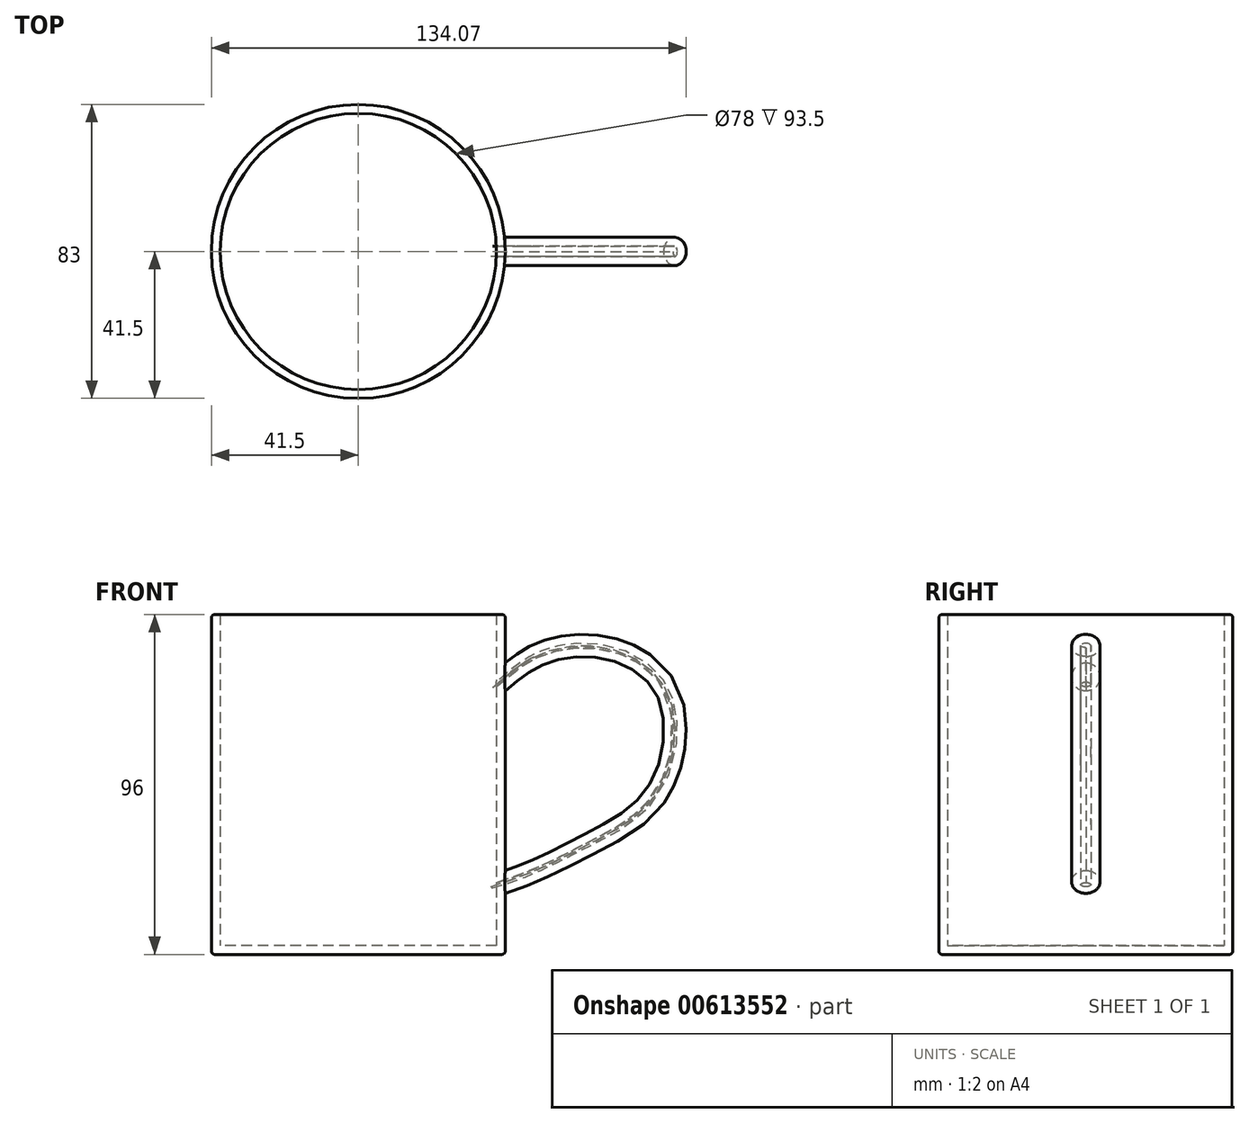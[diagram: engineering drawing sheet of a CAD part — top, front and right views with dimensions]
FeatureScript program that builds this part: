
annotation { "Feature Type Name" : "Feature", "Feature Type Description" : "" }
export const myFeature = defineFeature(function(context is Context, id is Id, definition is map)
    precondition{}
    {
        {
            var Q0;
            Q0=qCreatedBy(makeId("Top.planeOp"),FACE);
            var sketch = newSketch(context, id + "F0", { "sketchPlane" : qUnion([Q0])});
            skCircle(sketch, "E0", {"center": v(0, 0) * mm, "radius": 41.5 * mm});
            skSolve(sketch);
        }
        {
            var Q0;
            Q0 = qSketchRegion(id + "F0", true);
            extrude(context, id + "F1", {"entities" : qUnion([Q0]), "depth" : 96 * mm, "offsetDistance" : 25 * mm});
        }
        {
            var Q0;
            Q0=qCreatedBy(makeId("Front.planeOp"),FACE);
            var sketch = newSketch(context, id + "F2", { "sketchPlane" : qUnion([Q0])});
            skFitSpline(sketch, "E1", {"points": [v(40.8, 76.01) * mm, v(51.05, 83.15) * mm, v(68.43, 85.37) * mm, v(85.82, 73.78) * mm, v(83.6, 47.03) * mm, v(65.31, 32.77) * mm, v(47.93, 24.3) * mm, v(37.67, 20.73) * mm], "startDerivative": vector(78.69, 67.2) * mm, "endDerivative": vector(-88.22, -27.19) * mm});
            skSolve(sketch);
        }
        {
            var Q0;
            Q0=qCreatedBy(makeId("Right.planeOp"),FACE);
            cPlane(context, id + "F3", {"entities" : qUnion([Q0]), "cplaneType" : CPlaneType.OFFSET, "offset" : 41.5 * mm, "width" : 150 * mm, "height" : 150 * mm});
        }
        {
            var Q0;
            Q0=qCreatedBy(id+"F3.planeOp",FACE);
            var sketch = newSketch(context, id + "F4", { "sketchPlane" : qUnion([Q0])});
            skCircle(sketch, "E2", {"center": v(0, 78.39) * mm, "radius": 4 * mm});
            skSolve(sketch);
        }
        {
            var Q0;
            Q0=makeQuery(id+"F4.imprint","IMPRINT",FACE,{"disambiguationData":[TD([[makeQuery(id+"F4.imprint","IMPRINT",EDGE,{"derivedFrom":sQuery(id+"F4.wireOp",EDGE,"E2")}),1.0]])]});
            var Q1;
            Q1=sQuery(id+"F2.wireOp",EDGE,"E1");
            sweep(context, id + "F5", {"operationType" : NewBodyOperationType.ADD, "profiles" : qUnion([Q0]), "path" : qUnion([Q1])});
        }
        {
            var Q0;
            Q0=makeQuery(id+"F1.opExtrude","CAP_FACE",FACE,{"disambiguationData":[OSD([sQuery(id+"F0.wireOp",EDGE,"E0")])],"isStart":false});
            shell(context, id + "F6", {"entities" : qUnion([Q0]), "thickness" : 2.5 * mm});
        }
        {
            var Q0;
            Q0=makeQuery(id+"F1.opExtrude","CAP_EDGE",EDGE,{"disambiguationData":[OSD([sQuery(id+"F0.wireOp",EDGE,"E0")])],"isStart":false});
            fillet(context, id + "F7", {"entities" : qUnion([Q0]), "radius" : 1 * mm, "tangentPropagation" : true, "allowEdgeOverflow" : false});
        }
        {
            var Q0;
            Q0=makeQuery(id+"F1.opExtrude","CAP_EDGE",EDGE,{"disambiguationData":[OSD([sQuery(id+"F0.wireOp",EDGE,"E0")])],"isStart":true});
            fillet(context, id + "F8", {"entities" : qUnion([Q0]), "radius" : 1 * mm, "tangentPropagation" : true, "allowEdgeOverflow" : false});
        }
    });
